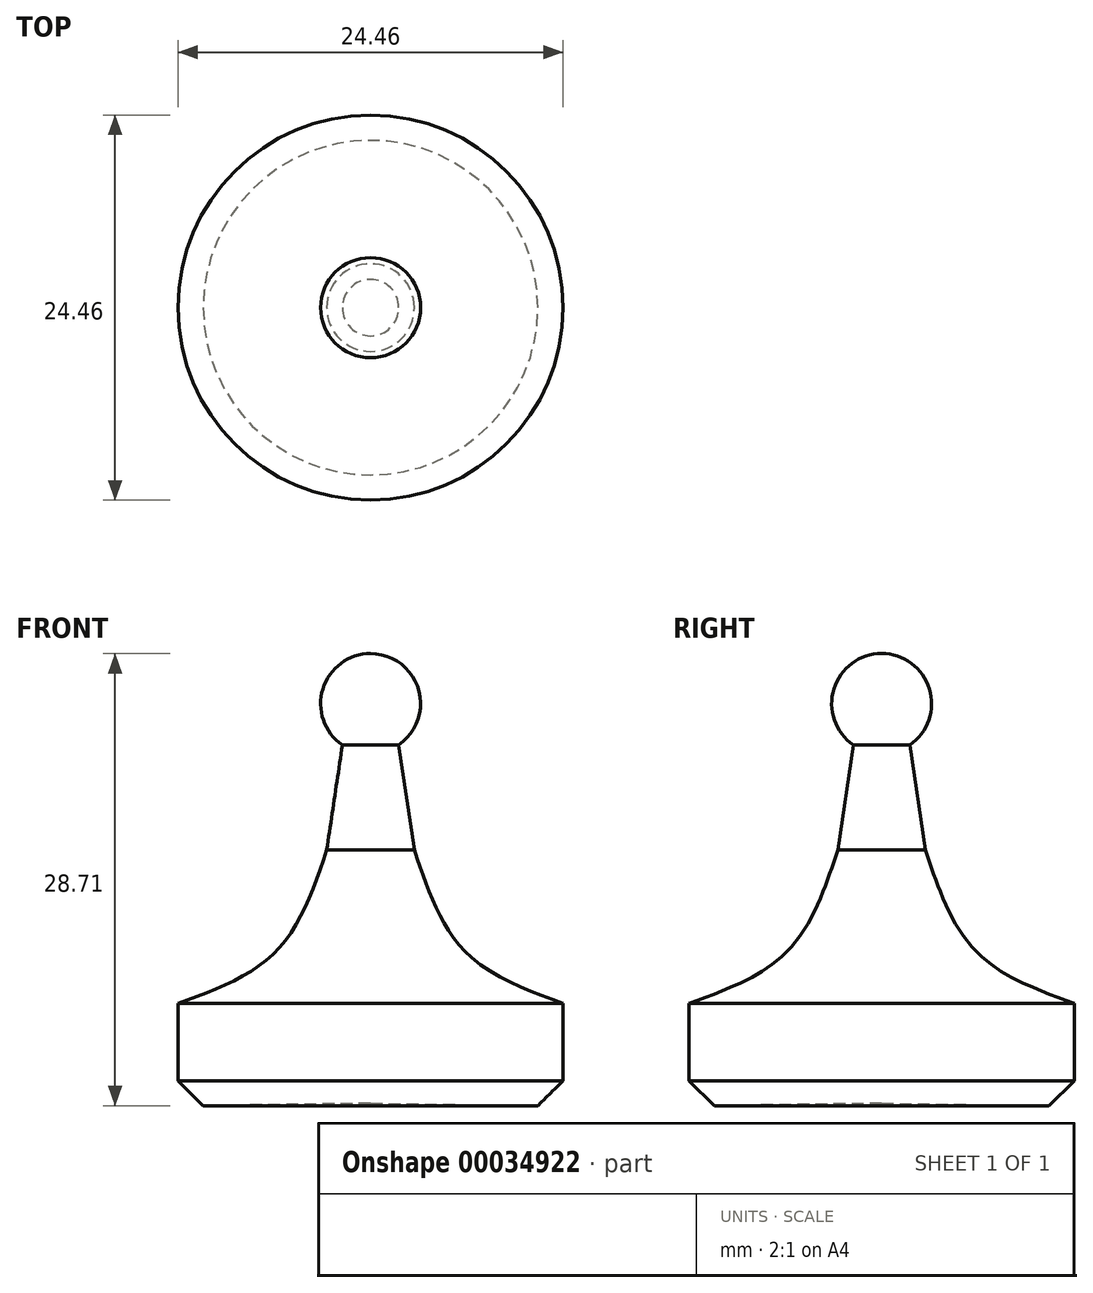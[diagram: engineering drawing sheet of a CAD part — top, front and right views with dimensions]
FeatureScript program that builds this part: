
annotation { "Feature Type Name" : "Feature", "Feature Type Description" : "" }
export const myFeature = defineFeature(function(context is Context, id is Id, definition is map)
    precondition{}
    {
        {
            var Q0;
            Q0=qCreatedBy(makeId("Front.planeOp"),FACE);
            var sketch = newSketch(context, id + "F0", { "sketchPlane" : qUnion([Q0])});
            skLineSegment(sketch, "E0", {"start": v(0, 14.36) * mm, "end": v(0, -11.04) * mm, "construction": true});
            skArc(sketch, "E1", {"start": v(1.8, 11.74) * mm, "mid": v(3.03, 15.3) * mm, "end": v(0, 17.53) * mm});
            skLineSegment(sketch, "E2", {"start": v(1.8, 11.74) * mm, "end": v(2.78, 5.05) * mm});
            skLineSegment(sketch, "E3", {"start": v(12.23, -4.68) * mm, "end": v(12.23, -11.2) * mm});
            skLineSegment(sketch, "E4", {"start": v(12.23, -11.2) * mm, "end": v(0, -11.04) * mm});
            skFitSpline(sketch, "E5", {"points": [v(2.78, 5.05) * mm, v(6, -1.38) * mm, v(12.23, -4.68) * mm], "startDerivative": vector(4.86, -14.34) * mm, "endDerivative": vector(14.05, -5.11) * mm});
            skLineSegment(sketch, "E6", {"start": v(0, -11.04) * mm, "end": v(0, 17.53) * mm});
            skSolve(sketch);
        }
        {
            var Q0;
            Q0=makeQuery(id+"F0.imprint","IMPRINT",FACE,{"disambiguationData":[TD([[makeQuery(id+"F0.imprint","IMPRINT",EDGE,{"derivedFrom":sQuery(id+"F0.wireOp",EDGE,"E1")}),1.0]])]});
            var Q1;
            Q1=sQuery(id+"F0.wireOp",EDGE,"E6");
            revolve(context, id + "F1", {"entities" : qUnion([Q0]), "axis" : qUnion([Q1]), "revolveType" : RevolveType.FULL});
        }
        {
            var Q0;
            Q0=makeQuery(id+"F1.opRevolve","SWEPT_EDGE",EDGE,{"disambiguationData":[OSD([sQuery(id+"F0.wireOp",EDGE,"E3"),sQuery(id+"F0.wireOp",EDGE,"E4")])]});
            chamfer(context, id + "F2", {"entities" : qUnion([Q0]), "width" : 1.59 * mm, "tangentPropagation" : true});
        }
    });
